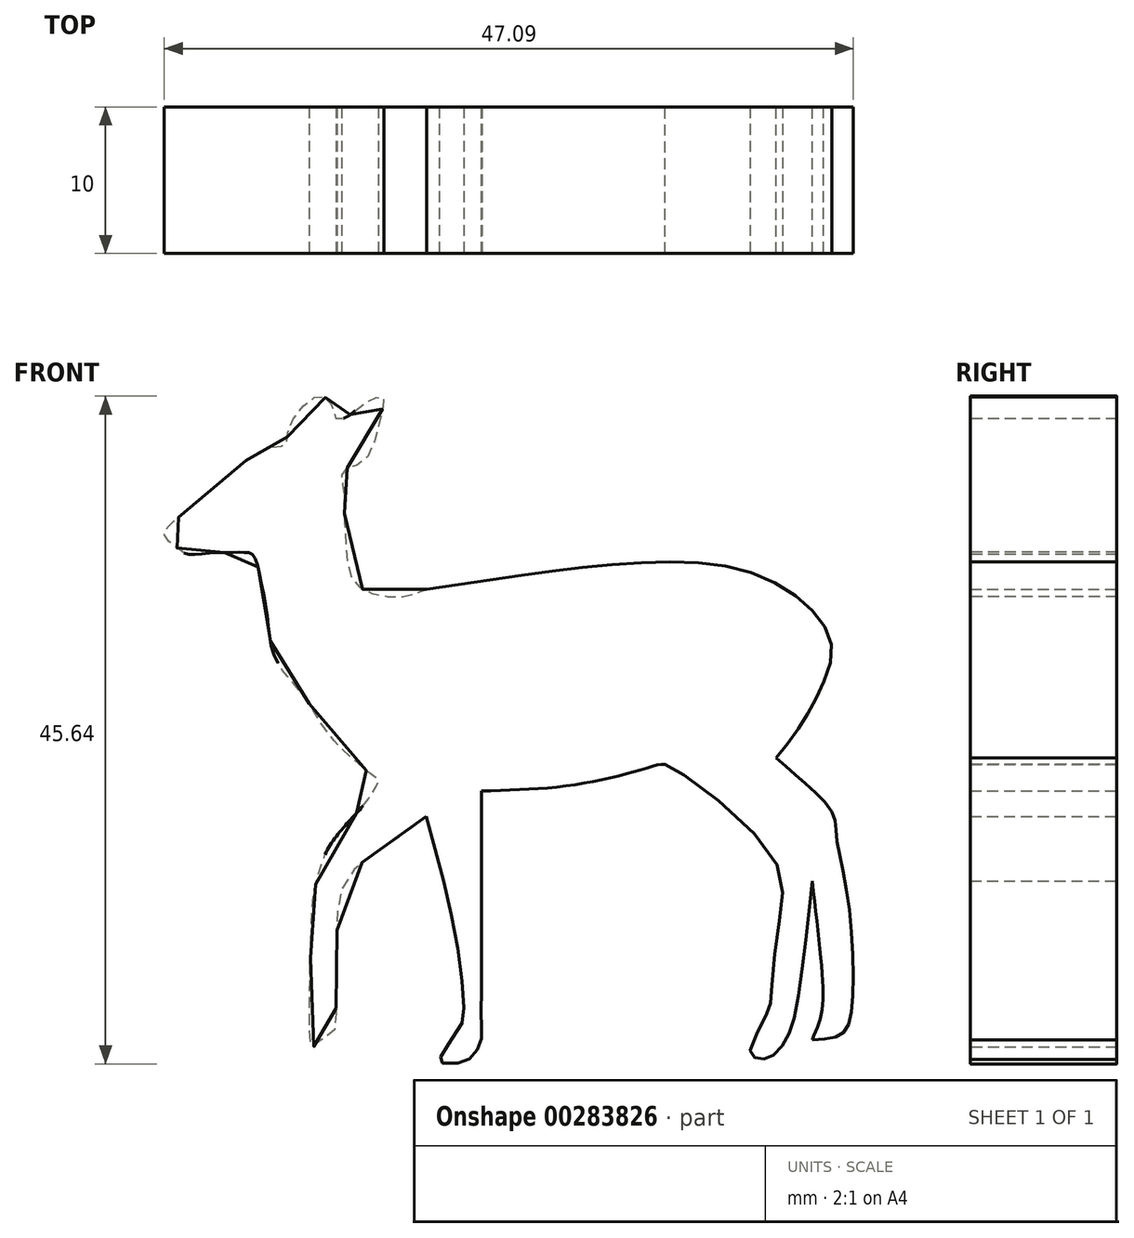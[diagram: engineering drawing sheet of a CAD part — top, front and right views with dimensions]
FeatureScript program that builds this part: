
annotation { "Feature Type Name" : "Feature", "Feature Type Description" : "" }
export const myFeature = defineFeature(function(context is Context, id is Id, definition is map)
    precondition{}
    {
        {
            var Q0;
            Q0=qCreatedBy(makeId("Front.planeOp"),FACE);
            var sketch = newSketch(context, id + "F0", { "sketchPlane" : qUnion([Q0])});
            skFitSpline(sketch, "E0", {"points": [v(26.1, -1.21) * mm, v(34.47, 0) * mm, v(41.87, 0.66) * mm, v(48.12, 0) * mm, v(52.37, -2.56) * mm, v(53.78, -5.27) * mm, v(52.95, -8.16) * mm, v(51.66, -10.48) * mm, v(49.99, -12.73) * mm], "startDerivative": vector(49.98, 7.6) * mm, "endDerivative": vector(-18.07, -23.03) * mm});
            skFitSpline(sketch, "E1", {"points": [v(49.99, -12.73) * mm, v(52.05, -14.54) * mm, v(53.85, -16.53) * mm, v(54.1, -18.08) * mm, v(54.9, -22.43) * mm, v(55.17, -29.72) * mm, v(54.44, -31.63) * mm, v(52.44, -32) * mm], "startDerivative": vector(14.76, -12.78) * mm, "endDerivative": vector(-19.7, -0.56) * mm});
            skFitSpline(sketch, "E2", {"points": [v(52.44, -32) * mm, v(53.02, -30.45) * mm, v(53.15, -27.94) * mm, v(52.44, -21.13) * mm], "startDerivative": vector(2.83, 6.36) * mm, "endDerivative": vector(-1.96, 15.92) * mm});
            skFitSpline(sketch, "E3", {"points": [v(52.44, -21.13) * mm, v(51.83, -26.64) * mm, v(51.2, -30.58) * mm, v(50.64, -32) * mm, v(49.92, -32.95) * mm, v(49.32, -33.29) * mm, v(48.76, -33.29) * mm, v(48.28, -33.01) * mm, v(48.32, -32.33) * mm, v(49.5, -29.8) * mm, v(49.6, -29.37) * mm, v(50.12, -24.37) * mm, v(49.48, -19.08) * mm, v(42.38, -13.18) * mm], "startDerivative": vector(-5.05, -47.94) * mm, "endDerivative": vector(-9.93, 0.28) * mm});
            skFitSpline(sketch, "E4", {"points": [v(42.38, -13.18) * mm, v(40.7, -13.55) * mm, v(35.9, -14.6) * mm, v(29.85, -15) * mm], "startDerivative": vector(-4.57, 0.86) * mm, "endDerivative": vector(-15.02, -0.59) * mm});
            skFitSpline(sketch, "E5", {"points": [v(29.85, -15) * mm, v(29.85, -27.85) * mm, v(29.85, -31.06) * mm, v(29.85, -32) * mm, v(29.3, -33.06) * mm, v(28.38, -33.55) * mm, v(27, -33.51) * mm, v(27.27, -32.83) * mm, v(28.26, -31.26) * mm, v(28.57, -30.72) * mm, v(28.15, -25.32) * mm, v(26.07, -16.73) * mm], "startDerivative": vector(0.24, -73.8) * mm, "endDerivative": vector(-14.35, 51.3) * mm});
            skFitSpline(sketch, "E6", {"points": [v(26.07, -16.73) * mm, v(23.8, -18.42) * mm, v(20.55, -21.13) * mm, v(19.98, -24.16) * mm, v(19.98, -25.34) * mm, v(19.9, -29.7) * mm, v(19.67, -31.55) * mm, v(18.8, -32) * mm, v(18.3, -32.5) * mm, v(18.1, -28.6) * mm, v(18.33, -22.36) * mm, v(18.45, -21.7) * mm, v(19.33, -18.99) * mm, v(21.93, -15.77) * mm, v(22.81, -14.28) * mm, v(22.7, -14.13) * mm, v(19.75, -11.53) * mm, v(17.8, -8.62) * mm, v(15.83, -6.06) * mm, v(15.24, -3.28) * mm, v(14.65, 0) * mm, v(14.2, 1.18) * mm, v(13.65, 1.32) * mm, v(12.64, 1.32) * mm, v(10.78, 1.22) * mm, v(9.64, 1.22) * mm, v(8.87, 1.77) * mm, v(8.18, 2.45) * mm, v(8.41, 3.05) * mm, v(9.5, 4) * mm, v(13.04, 6.97) * mm, v(15.42, 8.52) * mm, v(16.45, 8.64) * mm, v(16.64, 9.67) * mm, v(18.25, 11.8) * mm, v(19.22, 11.86) * mm, v(19.8, 10.83) * mm, v(19.86, 10.51) * mm, v(20.5, 10.51) * mm, v(21.73, 11.41) * mm, v(23.08, 11.93) * mm, v(23.02, 10.83) * mm, v(21.73, 7.49) * mm, v(20.38, 6.9) * mm, v(20.38, 5.88) * mm, v(20.44, 5.43) * mm, v(20.63, 1.11) * mm, v(21.53, -1.08) * mm, v(24.17, -1.72) * mm, v(26.1, -1.21) * mm], "startDerivative": vector(-80.83, -65.25) * mm, "endDerivative": vector(83.35, 33.36) * mm});
            skSolve(sketch);
        }
        {
            var Q0;
            Q0=makeQuery(id+"F0.imprint","IMPRINT",FACE,{"disambiguationData":[TD([[makeQuery(id+"F0.imprint","IMPRINT",EDGE,{"derivedFrom":sQuery(id+"F0.wireOp",EDGE,"E0")}),-1.0]])]});
            extrude(context, id + "F1", {"entities" : qUnion([Q0]), "depth" : 10 * mm});
        }
    });
